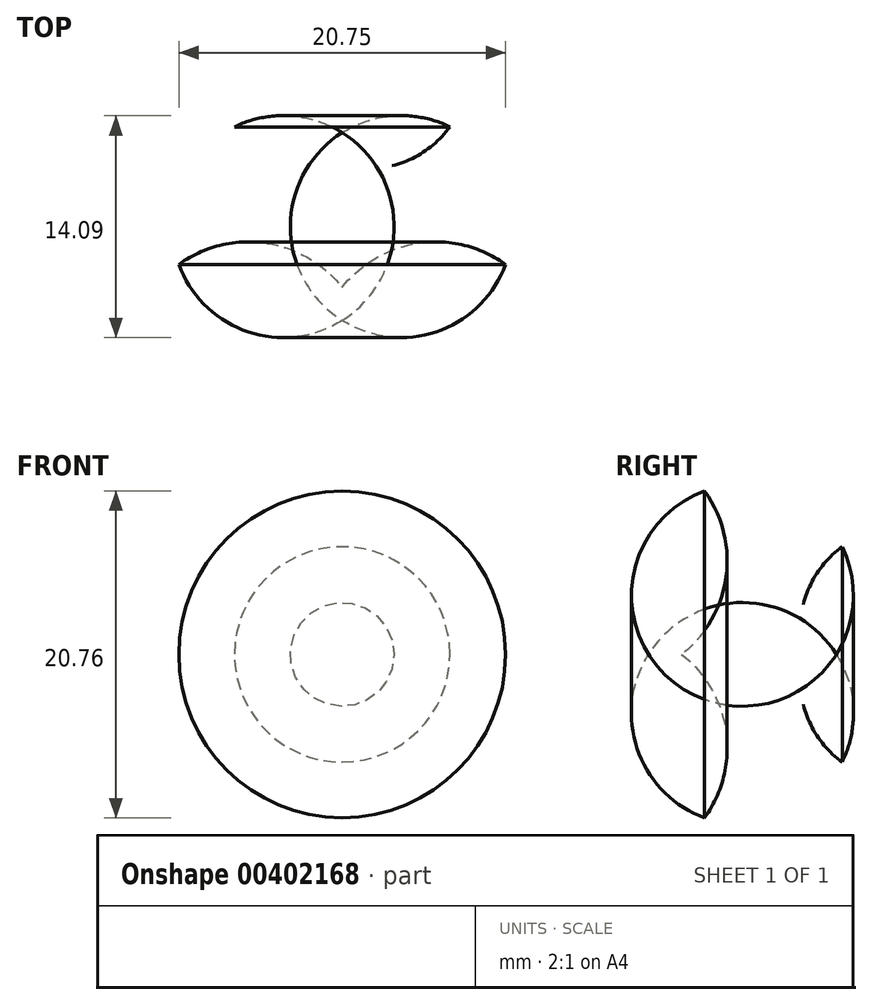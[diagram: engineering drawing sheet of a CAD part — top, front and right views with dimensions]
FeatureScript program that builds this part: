
annotation { "Feature Type Name" : "Feature", "Feature Type Description" : "" }
export const myFeature = defineFeature(function(context is Context, id is Id, definition is map)
    precondition{}
    {
        {
            var Q0;
            Q0=qCreatedBy(makeId("Top.planeOp"),FACE);
            var sketch = newSketch(context, id + "F0", { "sketchPlane" : qUnion([Q0])});
            skLineSegment(sketch, "E0", {"start": v(-16.38, 46.79) * mm, "end": v(-16.38, 17.08) * mm});
            skArc(sketch, "E1", {"start": v(-16.38, 26.44) * mm, "mid": v(-29.9, 21.76) * mm, "end": v(-16.38, 17.08) * mm});
            skArc(sketch, "E2", {"start": v(-16.38, 36.26) * mm, "mid": v(-27.18, 30.3) * mm, "end": v(-16.38, 24.33) * mm});
            skArc(sketch, "E3", {"start": v(-16.38, 46.79) * mm, "mid": v(-24.47, 40.47) * mm, "end": v(-16.38, 34.16) * mm});
            skSolve(sketch);
        }
        {
            var Q0;
            Q0 = qSketchRegion(id + "F0", true);
            var Q1;
            Q1=sQuery(id+"F0.wireOp",EDGE,"E0");
            revolve(context, id + "F1", {"entities" : qUnion([Q0]), "axis" : qUnion([Q1]), "revolveType" : RevolveType.FULL});
        }
    });
